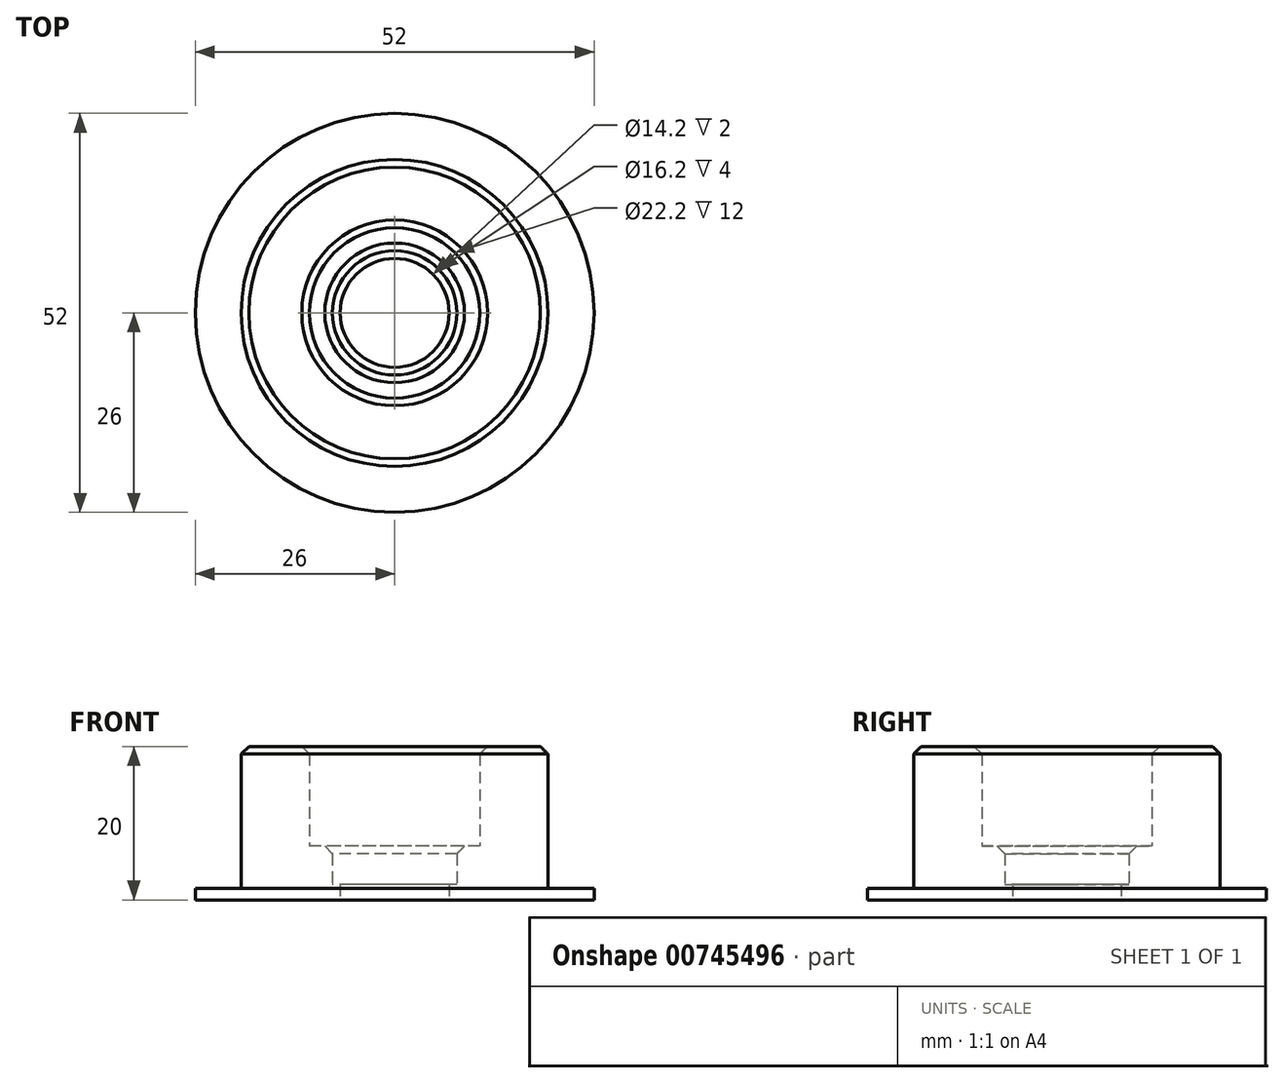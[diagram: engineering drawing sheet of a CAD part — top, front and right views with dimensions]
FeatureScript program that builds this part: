
annotation { "Feature Type Name" : "Feature", "Feature Type Description" : "" }
export const myFeature = defineFeature(function(context is Context, id is Id, definition is map)
    precondition{}
    {
        {
            var Q0;
            Q0=qCreatedBy(makeId("Top.planeOp"),FACE);
            var sketch = newSketch(context, id + "F0", { "sketchPlane" : qUnion([Q0])});
            skCircle(sketch, "E0", {"center": v(0, 0) * mm, "radius": 2.6 * mm});
            skCircle(sketch, "E1", {"center": v(0, 0) * mm, "radius": 8.1 * mm});
            skCircle(sketch, "E2", {"center": v(0, 0) * mm, "radius": 20 * mm});
            skCircle(sketch, "E3.0", {"center": v(0, 0) * mm, "radius": 11.1 * mm});
            skCircle(sketch, "E4", {"center": v(0, 0) * mm, "radius": 7.1 * mm});
            skCircle(sketch, "E5.0", {"center": v(0, 0) * mm, "radius": 26 * mm});
            skSolve(sketch);
        }
        {
            var Q0;
            Q0=makeQuery(id+"F0.imprint","IMPRINT",FACE,{"disambiguationData":[TD([[makeQuery(id+"F0.imprint","IMPRINT",EDGE,{"derivedFrom":sQuery(id+"F0.wireOp",EDGE,"E1")}),1.0]])]});
            extrude(context, id + "F1", {"entities" : qUnion([Q0]), "depth" : 2 * mm, "offsetDistance" : 25 * mm});
        }
        {
            var Q0;
            Q0=makeQuery(id+"F0.imprint","IMPRINT",FACE,{"disambiguationData":[TD([[makeQuery(id+"F0.imprint","IMPRINT",EDGE,{"derivedFrom":sQuery(id+"F0.wireOp",EDGE,"E1")}),-1.0]])]});
            extrude(context, id + "F2", {"entities" : qUnion([Q0]), "operationType" : NewBodyOperationType.ADD, "depth" : 7 * mm, "offsetDistance" : 25 * mm});
        }
        {
            var Q0;
            Q0=makeQuery(id+"F0.imprint","IMPRINT",FACE,{"disambiguationData":[TD([[makeQuery(id+"F0.imprint","IMPRINT",EDGE,{"derivedFrom":sQuery(id+"F0.wireOp",EDGE,"E2")}),1.0]])]});
            extrude(context, id + "F3", {"entities" : qUnion([Q0]), "operationType" : NewBodyOperationType.ADD, "depth" : 20 * mm, "offsetDistance" : 25 * mm});
        }
        {
            var Q0;
            Q0=makeQuery(id+"F0.imprint","IMPRINT",FACE,{"disambiguationData":[TD([[makeQuery(id+"F0.imprint","IMPRINT",EDGE,{"derivedFrom":sQuery(id+"F0.wireOp",EDGE,"E2")}),-1.0]])]});
            extrude(context, id + "F4", {"entities" : qUnion([Q0]), "operationType" : NewBodyOperationType.ADD, "depth" : 1.5 * mm, "offsetDistance" : 25 * mm});
        }
        {
            var Q0;
            Q0=makeQuery(id+"F3.opExtrude","CAP_FACE",FACE,{"disambiguationData":[OSD([sQuery(id+"F0.wireOp",EDGE,"E2"),sQuery(id+"F0.wireOp",EDGE,"E3.0")])],"isStart":false});
            var Q1;
            Q1=makeQuery(id+"F2.opExtrude","CAP_EDGE",EDGE,{"disambiguationData":[OSD([sQuery(id+"F0.wireOp",EDGE,"E1")])],"isStart":false});
            chamfer(context, id + "F5", {"entities" : qUnion([Q0, Q1]), "width" : 1 * mm, "tangentPropagation" : true});
        }
    });
